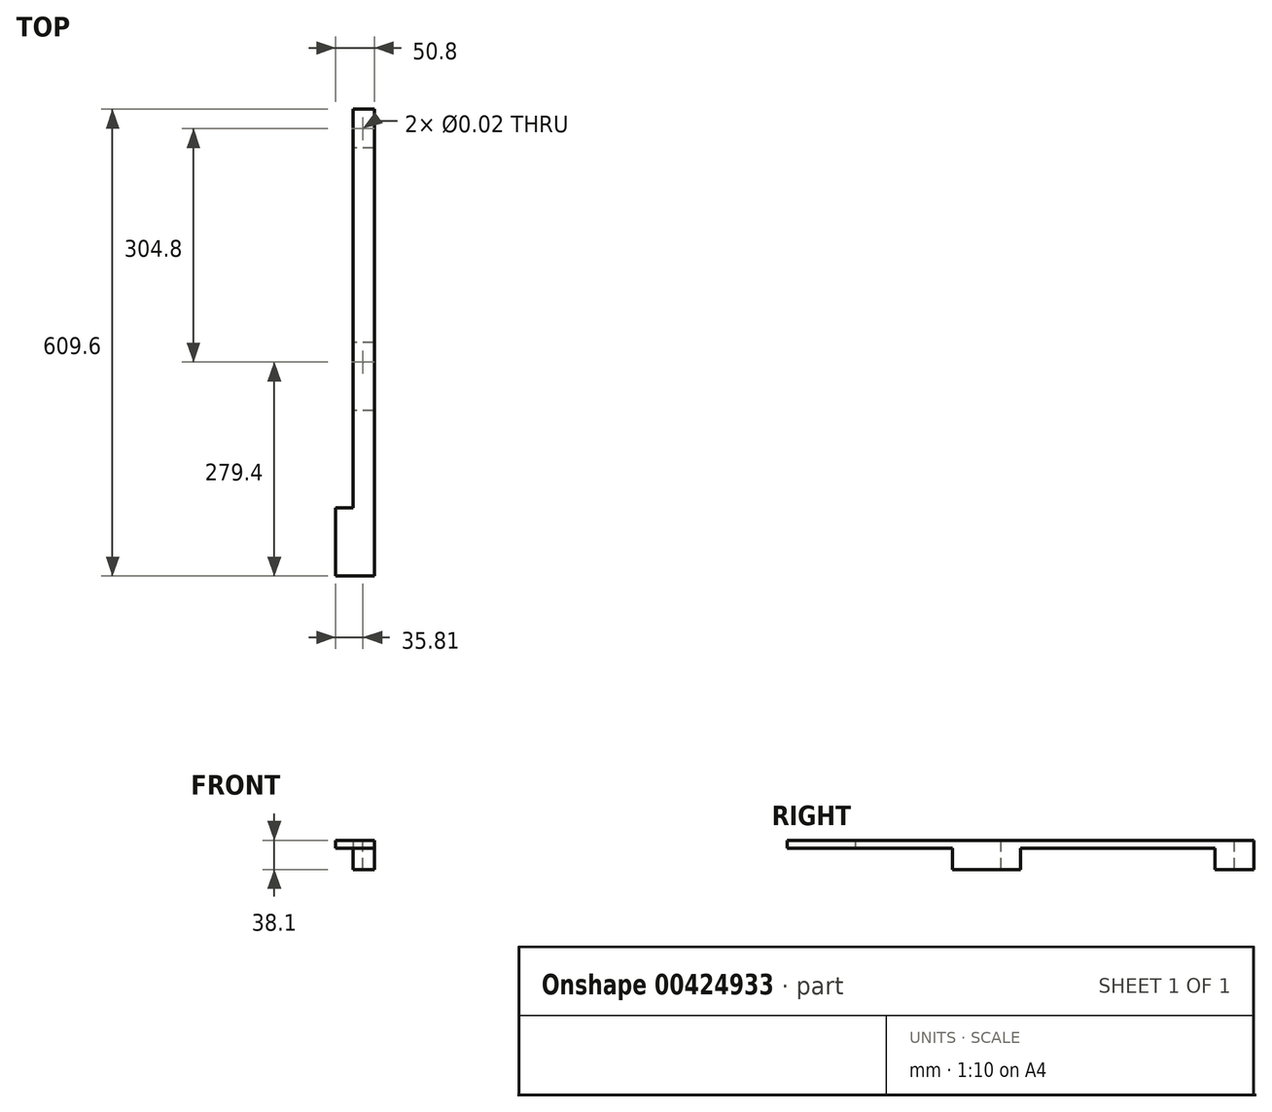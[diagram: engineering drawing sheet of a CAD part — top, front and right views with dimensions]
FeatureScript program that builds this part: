
annotation { "Feature Type Name" : "Feature", "Feature Type Description" : "" }
export const myFeature = defineFeature(function(context is Context, id is Id, definition is map)
    precondition{}
    {
        {
            var Q0;
            Q0=qCreatedBy(makeId("Front.planeOp"),FACE);
            var sketch = newSketch(context, id + "F0", { "sketchPlane" : qUnion([Q0])});
            skLineSegment(sketch, "E0", {"start": v(0, 0) * mm, "end": v(27.69, 0) * mm});
            skLineSegment(sketch, "E1", {"start": v(27.69, 0) * mm, "end": v(27.69, 38.1) * mm});
            skLineSegment(sketch, "E2", {"start": v(27.69, 38.1) * mm, "end": v(-23.11, 38.1) * mm});
            skLineSegment(sketch, "E3", {"start": v(-23.11, 38.1) * mm, "end": v(-23.11, 27.94) * mm});
            skLineSegment(sketch, "E4", {"start": v(-23.11, 27.94) * mm, "end": v(0, 27.94) * mm});
            skLineSegment(sketch, "E5", {"start": v(0, 27.94) * mm, "end": v(0, 0) * mm});
            skSolve(sketch);
        }
        {
            var Q0;
            Q0=makeQuery(id+"F0.imprint","IMPRINT",FACE,{"disambiguationData":[TD([[makeQuery(id+"F0.imprint","IMPRINT",EDGE,{"derivedFrom":sQuery(id+"F0.wireOp",EDGE,"E0")}),1.0]])]});
            extrude(context, id + "F1", {"entities" : qUnion([Q0]), "depth" : 609.6 * mm, "symmetric" : true});
        }
        {
            var Q0;
            Q0=makeQuery(id+"F1.opExtrude","SWEPT_FACE",FACE,{"disambiguationData":[OSD([sQuery(id+"F0.wireOp",EDGE,"E0")])]});
            var sketch = newSketch(context, id + "F2", { "sketchPlane" : qUnion([Q0])});
            skLineSegment(sketch, "E6", {"start": v(12.7, -279.4) * mm, "end": v(12.7, 25.4) * mm, "construction": true});
            skSolve(sketch);
        }
        {
            var Q0;
            Q0=sQuery(id+"F2.wireOp",VERTEX,"E6.end");
            var Q1;
            Q1=sQuery(id+"F2.wireOp",VERTEX,"E6.start");
            var Q2;
            Q2=makeQuery(id+"F1.opExtrude","SWEPT_BODY",BODY,{"disambiguationData":[OSD([sQuery(id+"F0.wireOp",EDGE,"E0"),sQuery(id+"F0.wireOp",EDGE,"E1"),sQuery(id+"F0.wireOp",EDGE,"E2"),sQuery(id+"F0.wireOp",EDGE,"E3"),sQuery(id+"F0.wireOp",EDGE,"E4"),sQuery(id+"F0.wireOp",EDGE,"E5")])]});
            hole(context, id + "F3", {"style" : HoleStyle.SIMPLE, "endStyle" : HoleEndStyle.THROUGH, "standardTappedOrClearance" : lookupTablePath({ "standard" : "ANSI", "size" : "1/2 (0.5)", "type" : "Drilled" }), "standardBlindInLast" : lookupTablePath({ "standard" : "ANSI", "size" : "1/2", "type" : "Drilled" }), "holeDiameter" : 1 / 50.8 * mm, "isTappedThrough" : true, "tappedDepth" : 22.25 * mm, "tapClearance" : 3, "locations" : qUnion([Q0, Q1]), "scope" : qUnion([Q2]), "startStyle" : HoleStartStyle.SKETCH});
        }
        {
            var Q0;
            Q0=makeQuery(id+"F1.opExtrude","SWEPT_FACE",FACE,{"disambiguationData":[OSD([sQuery(id+"F0.wireOp",EDGE,"E0")])]});
            var sketch = newSketch(context, id + "F4", { "sketchPlane" : qUnion([Q0])});
            skLineSegment(sketch, "E7.bottom", {"start": v(27.69, 304.8) * mm, "end": v(0, 304.8) * mm});
            skLineSegment(sketch, "E7.top", {"start": v(27.69, 88.9) * mm, "end": v(0, 88.9) * mm});
            skLineSegment(sketch, "E7.left", {"start": v(27.69, 304.8) * mm, "end": v(27.69, 88.9) * mm});
            skLineSegment(sketch, "E7.right", {"start": v(0, 304.8) * mm, "end": v(0, 88.9) * mm});
            skLineSegment(sketch, "E8.bottom", {"start": v(27.69, 0) * mm, "end": v(0, 0) * mm});
            skLineSegment(sketch, "E8.top", {"start": v(27.69, -254) * mm, "end": v(0, -254) * mm});
            skLineSegment(sketch, "E8.left", {"start": v(27.69, 0) * mm, "end": v(27.69, -254) * mm});
            skLineSegment(sketch, "E8.right", {"start": v(0, 0) * mm, "end": v(0, -254) * mm});
            skSolve(sketch);
        }
        {
            var Q0;
            Q0 = qSketchRegion(id + "F4", true);
            var Q1;
            Q1=makeQuery(id+"F1.opExtrude","SWEPT_FACE",FACE,{"disambiguationData":[OSD([sQuery(id+"F0.wireOp",EDGE,"E4")])]});
            extrude(context, id + "F5", {"entities" : qUnion([Q0]), "operationType" : NewBodyOperationType.REMOVE, "endBound" : BoundingType.UP_TO_SURFACE, "oppositeDirection" : true, "endBoundEntityFace" : qUnion([Q1]), "depth" : 25.4 * mm});
        }
        {
            var Q0;
            {var subQ0=sQuery(id+"F0.wireOp",EDGE,"E4");Q0=makeQuery(id+"F5.boolean.opBoolean","MERGE",FACE,{"derivedFrom":[makeQuery(id+"F1.opExtrude","SWEPT_FACE",FACE,{"disambiguationData":[OSD([subQ0])]}),makeQuery(id+"F5.opExtrude","CAP_FACE",FACE,{"disambiguationData":[OSD([subQ0]),ownerDisambiguation([makeQuery(id+"F4.imprint","IMPRINT",EDGE,{"derivedFrom":sQuery(id+"F4.wireOp",EDGE,"E7.bottom")})])],"isStart":false}),makeQuery(id+"F5.opExtrude","CAP_FACE",FACE,{"disambiguationData":[OSD([subQ0]),ownerDisambiguation([makeQuery(id+"F4.imprint","IMPRINT",EDGE,{"derivedFrom":sQuery(id+"F4.wireOp",EDGE,"E8.bottom")})])],"isStart":false})]});}
            var sketch = newSketch(context, id + "F6", { "sketchPlane" : qUnion([Q0])});
            skLineSegment(sketch, "E9.bottom", {"start": v(-23.11, -304.8) * mm, "end": v(0, -304.8) * mm});
            skLineSegment(sketch, "E9.top", {"start": v(-23.11, 215.9) * mm, "end": v(0, 215.9) * mm});
            skLineSegment(sketch, "E9.left", {"start": v(-23.11, -304.8) * mm, "end": v(-23.11, 215.9) * mm});
            skLineSegment(sketch, "E9.right", {"start": v(0, -304.8) * mm, "end": v(0, 215.9) * mm});
            skSolve(sketch);
        }
        {
            var Q0;
            Q0 = qSketchRegion(id + "F6", true);
            extrude(context, id + "F7", {"entities" : qUnion([Q0]), "operationType" : NewBodyOperationType.REMOVE, "endBound" : BoundingType.THROUGH_ALL, "oppositeDirection" : true, "depth" : 25.4 * mm});
        }
    });
